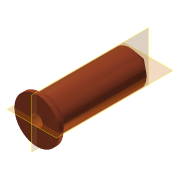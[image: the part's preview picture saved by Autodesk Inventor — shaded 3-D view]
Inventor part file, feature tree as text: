
AUTODESK INVENTOR PART (.ipt)
format: ipt  version: 2014 (Build 180170000, 170)  size: 154,624 bytes
history: native  units: mm
features: sketch x5, extrude x3, revolve x2, chamfer x1
ambient origin geometry x8: Origin, YZ Plane, XZ Plane, XY Plane, X Axis, Y Axis, Z Axis, Center Point
bodies: Solid1 (feature_tree)
feature tree (11):
  extrude  "Extrusion1"  Depth=1.0mm TaperAngle=0.0deg
  extrude  "Extrusion2"  Depth=15.437mm TaperAngle=0.0deg
  extrude  "Extrusion3"  Depth=21.0mm TaperAngle=0.0deg
  revolve  "Revolution1"  [1 undecoded]
  revolve  "Revolution2"  Angle=90.0deg
  chamfer  "Chamfer1"  Distance=0.7mm
  sketch  "Sketch1"  dims[d0=8.0mm d1=1.0mm d2=0.0mm]
  sketch  "Sketch2"  dims[d3=6.0mm d4=15.437mm d5=0.0mm]
  sketch  "Sketch3"  dims[d6=2.0mm d7=21.0mm d8=0.0mm]
  sketch  "Sketch4"  dims[d9=6.981317mm d10=0.2mm]
  sketch  "Sketch5"  dims[d11=30.0deg d13=90.0deg d14=0.7mm d15=90.0deg d16=0.3mm d17=2.0mm d18=45.0deg d19=45.0deg d21=0.125mm d22=0.05mm]
note: 1 required parameter value undecoded (feature->parameter linkage not recoverable at this tier; creation-order binding heuristic only, values carry confidence <= 0.55)
